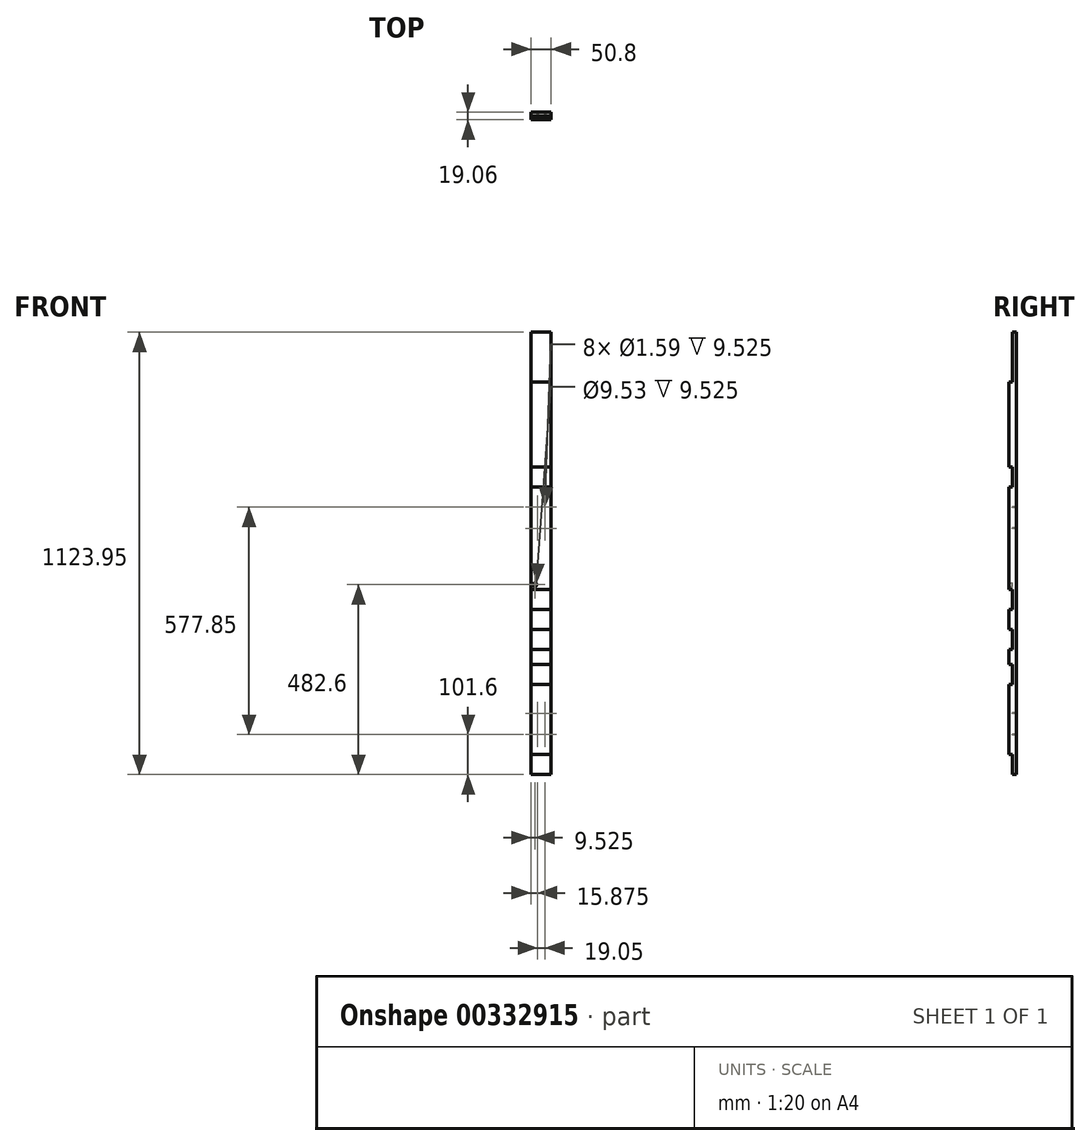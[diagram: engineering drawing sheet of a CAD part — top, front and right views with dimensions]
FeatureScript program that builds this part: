
annotation { "Feature Type Name" : "Feature", "Feature Type Description" : "" }
export const myFeature = defineFeature(function(context is Context, id is Id, definition is map)
    precondition{}
    {
        {
            var Q0;
            Q0=qCreatedBy(makeId("Top.planeOp"),FACE);
            var sketch = newSketch(context, id + "F0", { "sketchPlane" : qUnion([Q0])});
            skLineSegment(sketch, "E0.bottom", {"start": v(25.4, 9.53) * mm, "end": v(-25.4, 9.53) * mm});
            skLineSegment(sketch, "E0.top", {"start": v(25.4, -9.53) * mm, "end": v(-25.4, -9.53) * mm});
            skLineSegment(sketch, "E0.left", {"start": v(25.4, 9.53) * mm, "end": v(25.4, -9.52) * mm});
            skLineSegment(sketch, "E0.right", {"start": v(-25.4, 9.53) * mm, "end": v(-25.4, -9.53) * mm});
            skPoint(sketch, "E0.middle", {"position": v(0, 0) * mm});
            skSolve(sketch);
        }
        {
            var Q0;
            Q0=makeQuery(id+"F0.imprint","IMPRINT",FACE,{"disambiguationData":[TD([[makeQuery(id+"F0.imprint","IMPRINT",EDGE,{"derivedFrom":sQuery(id+"F0.wireOp",EDGE,"E0.bottom")}),1.0]])]});
            extrude(context, id + "F1", {"entities" : qUnion([Q0]), "depth" : 1123.95 * mm});
        }
        {
            var Q0;
            Q0=qCreatedBy(makeId("Front.planeOp"),FACE);
            var sketch = newSketch(context, id + "F2", { "sketchPlane" : qUnion([Q0])});
            skLineSegment(sketch, "E1.bottom", {"start": v(-38.77, 0) * mm, "end": v(83.66, 0) * mm});
            skLineSegment(sketch, "E1.top", {"start": v(-38.77, 50.8) * mm, "end": v(83.66, 50.8) * mm});
            skLineSegment(sketch, "E1.left", {"start": v(-38.77, 0) * mm, "end": v(-38.77, 50.8) * mm});
            skLineSegment(sketch, "E1.right", {"start": v(83.66, 0) * mm, "end": v(83.66, 50.8) * mm});
            skLineSegment(sketch, "E2.bottom", {"start": v(-59.18, 317.5) * mm, "end": v(49.65, 317.5) * mm});
            skLineSegment(sketch, "E2.top", {"start": v(-59.18, 368.3) * mm, "end": v(49.65, 368.3) * mm});
            skLineSegment(sketch, "E2.left", {"start": v(-59.18, 317.5) * mm, "end": v(-59.18, 368.3) * mm});
            skLineSegment(sketch, "E2.right", {"start": v(49.65, 317.5) * mm, "end": v(49.65, 368.3) * mm});
            skLineSegment(sketch, "E3.bottom", {"start": v(-44.21, 730.25) * mm, "end": v(49.65, 730.25) * mm});
            skLineSegment(sketch, "E3.top", {"start": v(-44.21, 781.05) * mm, "end": v(49.65, 781.05) * mm});
            skLineSegment(sketch, "E3.left", {"start": v(-44.21, 730.25) * mm, "end": v(-44.21, 781.05) * mm});
            skLineSegment(sketch, "E3.right", {"start": v(49.65, 730.25) * mm, "end": v(49.65, 781.05) * mm});
            skLineSegment(sketch, "E4.bottom", {"start": v(-74.14, 469.9) * mm, "end": v(71.42, 469.9) * mm});
            skLineSegment(sketch, "E4.top", {"start": v(-74.14, 419.1) * mm, "end": v(71.42, 419.1) * mm});
            skLineSegment(sketch, "E4.left", {"start": v(-74.14, 469.9) * mm, "end": v(-74.14, 419.1) * mm});
            skLineSegment(sketch, "E4.right", {"start": v(71.42, 469.9) * mm, "end": v(71.42, 419.1) * mm});
            skLineSegment(sketch, "E5.bottom", {"start": v(-210.36, 996.95) * mm, "end": v(132.8, 996.95) * mm});
            skLineSegment(sketch, "E5.top", {"start": v(-210.36, 1123.95) * mm, "end": v(132.8, 1123.95) * mm});
            skLineSegment(sketch, "E5.left", {"start": v(-210.36, 996.95) * mm, "end": v(-210.36, 1123.95) * mm});
            skLineSegment(sketch, "E5.right", {"start": v(132.8, 996.95) * mm, "end": v(132.8, 1123.95) * mm});
            skLineSegment(sketch, "E6.bottom", {"start": v(-90.73, 228.6) * mm, "end": v(65.12, 228.6) * mm});
            skLineSegment(sketch, "E6.top", {"start": v(-90.73, 279.4) * mm, "end": v(65.12, 279.4) * mm});
            skLineSegment(sketch, "E6.left", {"start": v(-90.73, 228.6) * mm, "end": v(-90.73, 279.4) * mm});
            skLineSegment(sketch, "E6.right", {"start": v(65.12, 228.6) * mm, "end": v(65.12, 279.4) * mm});
            skSolve(sketch);
        }
        {
            var Q0;
            Q0 = qSketchRegion(id + "F2", true);
            extrude(context, id + "F3", {"entities" : qUnion([Q0]), "operationType" : NewBodyOperationType.REMOVE, "depth" : 25.4 * mm});
        }
        {
            var Q0;
            Q0=qCreatedBy(makeId("Front.planeOp"),FACE);
            var sketch = newSketch(context, id + "F4", { "sketchPlane" : qUnion([Q0])});
            skCircle(sketch, "E7", {"center": v(9.52, 101.6) * mm, "radius": 0.8 * mm});
            skCircle(sketch, "E8", {"center": v(9.52, 155.58) * mm, "radius": 0.8 * mm});
            skCircle(sketch, "E9", {"center": v(9.52, 625.48) * mm, "radius": 0.8 * mm});
            skCircle(sketch, "E10", {"center": v(9.52, 679.45) * mm, "radius": 0.8 * mm});
            skLineSegment(sketch, "E11", {"start": v(0, 0) * mm, "end": v(0, 1192.46) * mm, "construction": true});
            skLineSegment(sketch, "E12.bottom", {"start": v(9.52, 101.6) * mm, "end": v(-9.52, 101.6) * mm, "construction": true});
            skLineSegment(sketch, "E12.top", {"start": v(9.52, 679.45) * mm, "end": v(-9.53, 679.45) * mm, "construction": true});
            skLineSegment(sketch, "E12.left", {"start": v(9.53, 101.6) * mm, "end": v(9.52, 679.45) * mm, "construction": true});
            skLineSegment(sketch, "E12.right", {"start": v(-9.52, 101.6) * mm, "end": v(-9.53, 679.45) * mm, "construction": true});
            skCircle(sketch, "E13", {"center": v(-9.53, 625.48) * mm, "radius": 0.8 * mm});
            skCircle(sketch, "E14", {"center": v(-9.53, 679.45) * mm, "radius": 0.8 * mm});
            skCircle(sketch, "E15", {"center": v(-9.52, 101.6) * mm, "radius": 0.8 * mm});
            skCircle(sketch, "E16", {"center": v(-9.52, 155.58) * mm, "radius": 0.8 * mm});
            skSolve(sketch);
        }
        {
            var Q0;
            Q0 = qSketchRegion(id + "F4", true);
            extrude(context, id + "F5", {"entities" : qUnion([Q0]), "operationType" : NewBodyOperationType.REMOVE, "oppositeDirection" : true, "depth" : 25.4 * mm});
        }
        {
            var Q0;
            Q0=qCreatedBy(makeId("Front.planeOp"),FACE);
            var sketch = newSketch(context, id + "F6", { "sketchPlane" : qUnion([Q0])});
            skCircle(sketch, "E17", {"center": v(15.88, 254) * mm, "radius": 4.76 * mm});
            skCircle(sketch, "E18", {"center": v(-15.88, 254) * mm, "radius": 4.76 * mm});
            skCircle(sketch, "E19", {"center": v(-15.88, 482.6) * mm, "radius": 4.76 * mm});
            skSolve(sketch);
        }
        {
            var Q0;
            Q0 = qSketchRegion(id + "F6", true);
            extrude(context, id + "F7", {"entities" : qUnion([Q0]), "operationType" : NewBodyOperationType.REMOVE, "depth" : 25.4 * mm});
        }
    });
